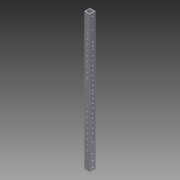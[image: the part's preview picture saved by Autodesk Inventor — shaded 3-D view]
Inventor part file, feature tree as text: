
AUTODESK INVENTOR PART (.ipt)
format: ipt  version: 2014 SP1 (Build 180222100, 222)  size: 270,336 bytes
history: native  units: in
note: dims shown in document units (in); Inventor stores cm internally (conversion verified against a paired STEP export)
features: extrude x4, sketch x4
ambient origin geometry x8: Origin, YZ Plane, XZ Plane, XY Plane, X Axis, Y Axis, Z Axis, Center Point
bodies: Solid1 (feature_tree)
feature tree (8):
  extrude  "Extrusion1"  Depth=1.0in
  extrude  "Extrusion2"  Depth=24.0in TaperAngle=0.0deg
  extrude  "Extrusion3"  Depth=0.26in
  extrude  "Extrusion4"  Depth=0.75in
  sketch  "Sketch1"  dims[d0=1.0in d1=1.0in]
  sketch  "Sketch2"  dims[d2=0.125in d3=24.0in d4=0.0in]
  sketch  "Sketch3"  dims[d5=0.55in d6=0.26in]
  sketch  "Sketch4"  dims[d7=24.0in d8=11.0236in d10=0.8481in d11=0.3937in d13=1.0in d15=1.0in d16=0.0in d17=1.75in d18=2.0in d19=1.75in d20=1.75in d21=0.26in d22=0.26in d23=0.26in d24=0.26in d25=0.26in d26=0.26in d27=0.26in d28=0.26in d29=1.0in d30=0.0in d31=2.0in d32=0.26in d33=0.26in d40=0.5in d41=0.26in d42=0.5in d43=0.26in d46=0.75in d47=0.75in d48=0.26in d49=0.26in d50=1.0in d51=0.0in d52=0.26in d53=5.5in d64=1.0in d65=0.26in d66=0.55in d67=24.0in d68=11.0236in d70=0.8481in d71=0.3937in d73=1.0in d76=0.375in d77=0.375in d85=0.5in d86=2.7559in d88=0.75in d89=0.3937in d91=1.0in d93=2.3622in d95=0.75in d96=0.3937in d98=1.0in d100=0.75in d101=0.75in]
